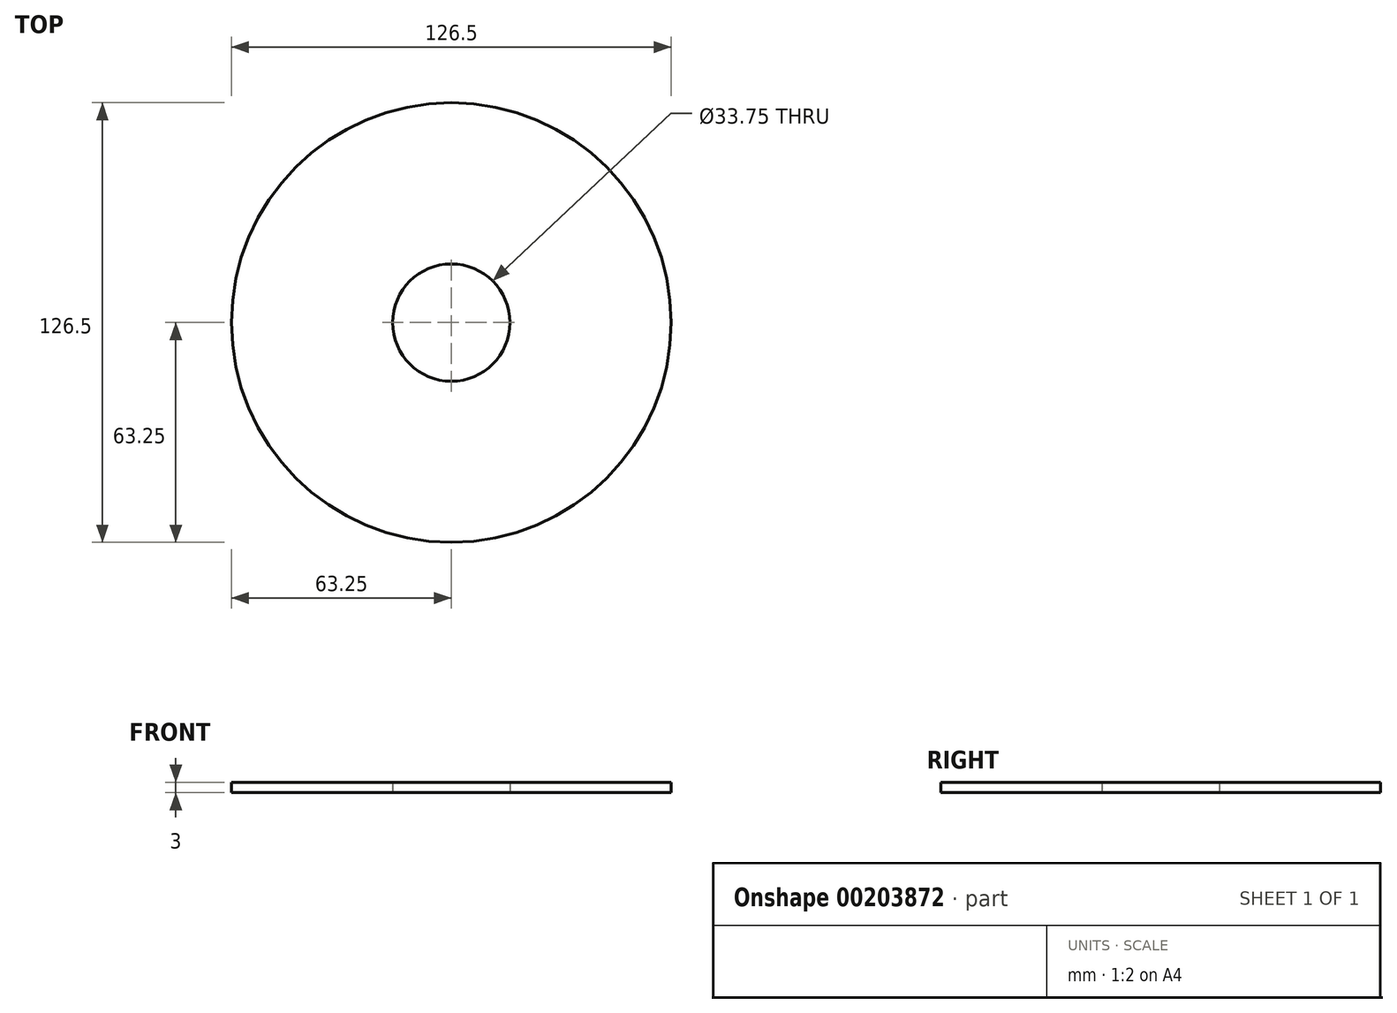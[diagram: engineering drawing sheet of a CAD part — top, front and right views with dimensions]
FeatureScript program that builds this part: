
annotation { "Feature Type Name" : "Feature", "Feature Type Description" : "" }
export const myFeature = defineFeature(function(context is Context, id is Id, definition is map)
    precondition{}
    {
        {
            var Q0;
            Q0=qCreatedBy(makeId("Top.planeOp"),FACE);
            var sketch = newSketch(context, id + "F0", { "sketchPlane" : qUnion([Q0])});
            skCircle(sketch, "E0", {"center": v(0, 0) * mm, "radius": 63.25 * mm});
            skCircle(sketch, "E1", {"center": v(0, 0) * mm, "radius": 16.88 * mm});
            skSolve(sketch);
        }
        {
            var Q0;
            Q0 = qSketchRegion(id + "F0", true);
            extrude(context, id + "F1", {"entities" : qUnion([Q0]), "depth" : 3 * mm});
        }
    });
